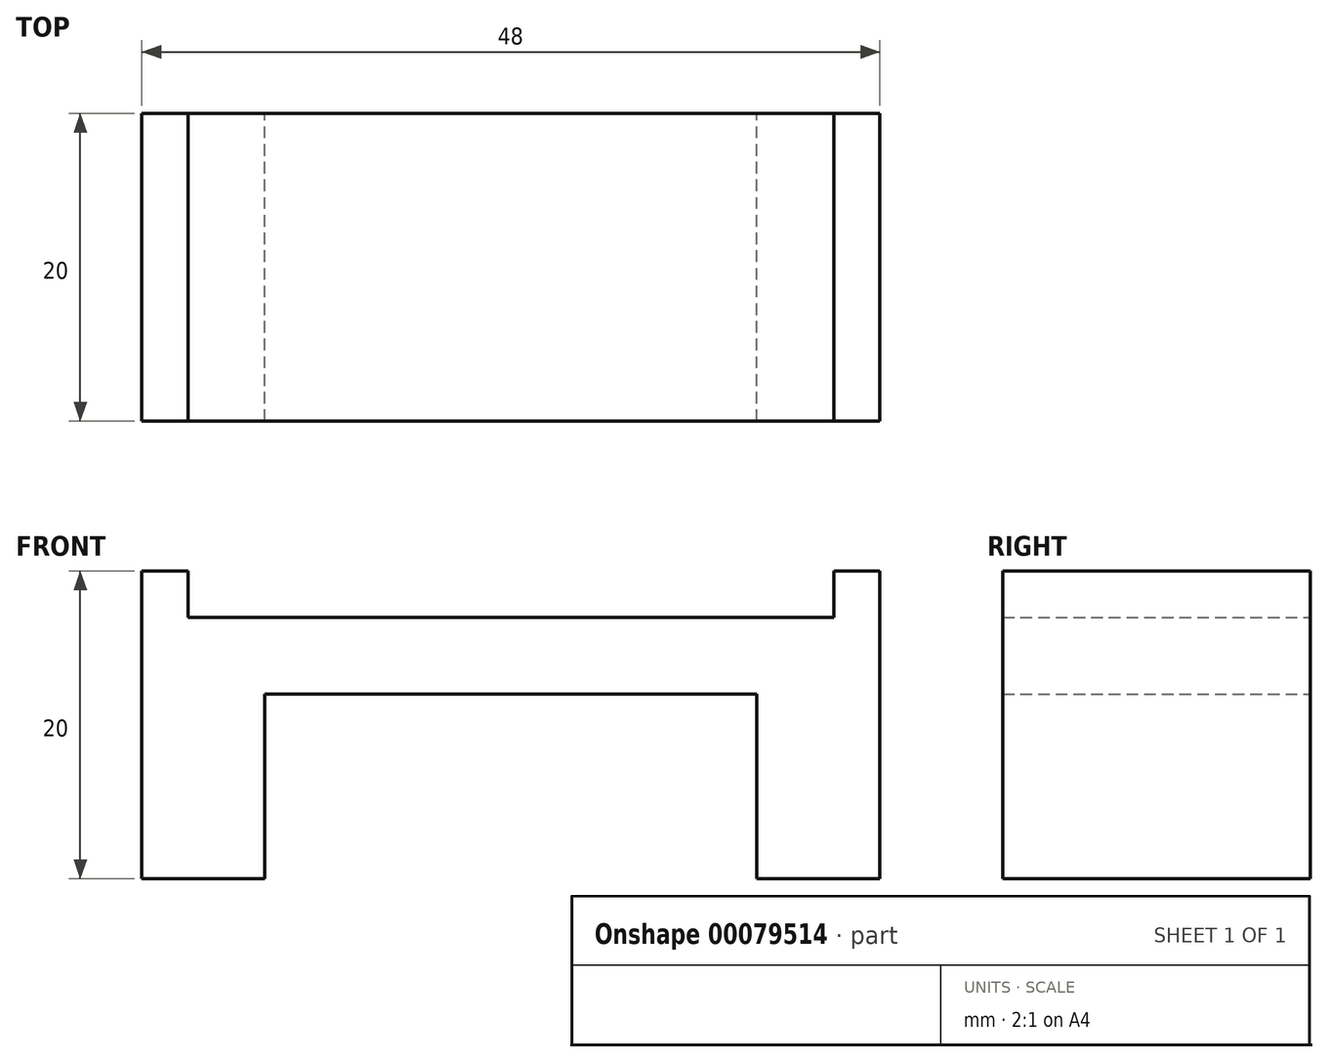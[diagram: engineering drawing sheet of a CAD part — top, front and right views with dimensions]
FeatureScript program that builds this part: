
annotation { "Feature Type Name" : "Feature", "Feature Type Description" : "" }
export const myFeature = defineFeature(function(context is Context, id is Id, definition is map)
    precondition{}
    {
        {
            var Q0;
            Q0=qCreatedBy(makeId("Front.planeOp"),FACE);
            var sketch = newSketch(context, id + "F0", { "sketchPlane" : qUnion([Q0])});
            skLineSegment(sketch, "E0", {"start": v(16, 0) * mm, "end": v(16, -12) * mm});
            skLineSegment(sketch, "E1", {"start": v(16, -12) * mm, "end": v(24, -12) * mm});
            skLineSegment(sketch, "E2", {"start": v(24, -12) * mm, "end": v(24, 8) * mm});
            skLineSegment(sketch, "E3", {"start": v(0, 38.31) * mm, "end": v(0, -27.34) * mm, "construction": true});
            skLineSegment(sketch, "E4.MirrorCS", {"start": v(-16, 0) * mm, "end": v(-16, -12) * mm});
            skLineSegment(sketch, "E5.MirrorCS", {"start": v(-16, -12) * mm, "end": v(-24, -12) * mm});
            skLineSegment(sketch, "E6.MirrorCS", {"start": v(-24, -12) * mm, "end": v(-24, 8) * mm});
            skLineSegment(sketch, "E7", {"start": v(-21, 5) * mm, "end": v(21, 5) * mm});
            skLineSegment(sketch, "E8", {"start": v(-16, 0) * mm, "end": v(16, 0) * mm});
            skLineSegment(sketch, "E9", {"start": v(-24, 8) * mm, "end": v(-21, 8) * mm});
            skLineSegment(sketch, "E10", {"start": v(-21, 8) * mm, "end": v(-21, 5) * mm});
            skLineSegment(sketch, "E11.MirrorCS", {"start": v(21, 8) * mm, "end": v(21, 5) * mm});
            skLineSegment(sketch, "E12.MirrorCS", {"start": v(24, 8) * mm, "end": v(21, 8) * mm});
            skSolve(sketch);
        }
        {
            var Q0;
            Q0=makeQuery(id+"F0.imprint","IMPRINT",FACE,{"disambiguationData":[TD([[makeQuery(id+"F0.imprint","IMPRINT",EDGE,{"derivedFrom":sQuery(id+"F0.wireOp",EDGE,"E0")}),1.0]])]});
            extrude(context, id + "F1", {"entities" : qUnion([Q0]), "depth" : 20 * mm});
        }
    });
